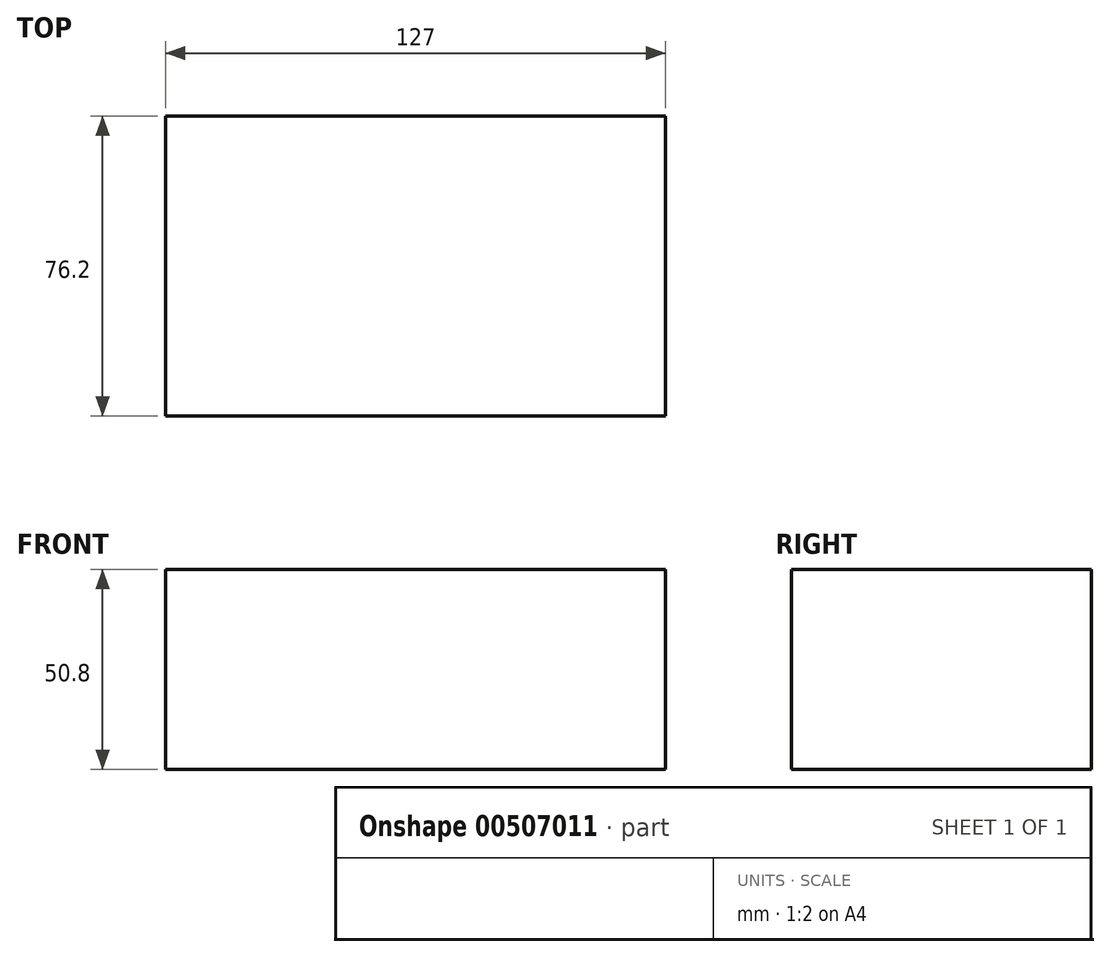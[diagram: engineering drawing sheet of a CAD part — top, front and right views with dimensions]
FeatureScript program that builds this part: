
annotation { "Feature Type Name" : "Feature", "Feature Type Description" : "" }
export const myFeature = defineFeature(function(context is Context, id is Id, definition is map)
    precondition{}
    {
        {
            var Q0;
            Q0=qCreatedBy(makeId("Front.planeOp"),FACE);
            var sketch = newSketch(context, id + "F0", { "sketchPlane" : qUnion([Q0])});
            skLineSegment(sketch, "E0.bottom", {"start": v(0, 0) * mm, "end": v(127, 0) * mm});
            skLineSegment(sketch, "E0.top", {"start": v(0, 50.8) * mm, "end": v(127, 50.8) * mm});
            skLineSegment(sketch, "E0.left", {"start": v(0, 0) * mm, "end": v(0, 50.8) * mm});
            skLineSegment(sketch, "E0.right", {"start": v(127, 0) * mm, "end": v(127, 50.8) * mm});
            skSolve(sketch);
        }
        {
            var Q0;
            Q0=makeQuery(id+"F0.imprint","IMPRINT",FACE,{"disambiguationData":[TD([[makeQuery(id+"F0.imprint","IMPRINT",EDGE,{"derivedFrom":sQuery(id+"F0.wireOp",EDGE,"E0.bottom")}),1.0]])]});
            extrude(context, id + "F1", {"entities" : qUnion([Q0]), "depth" : 76.2 * mm});
        }
    });
